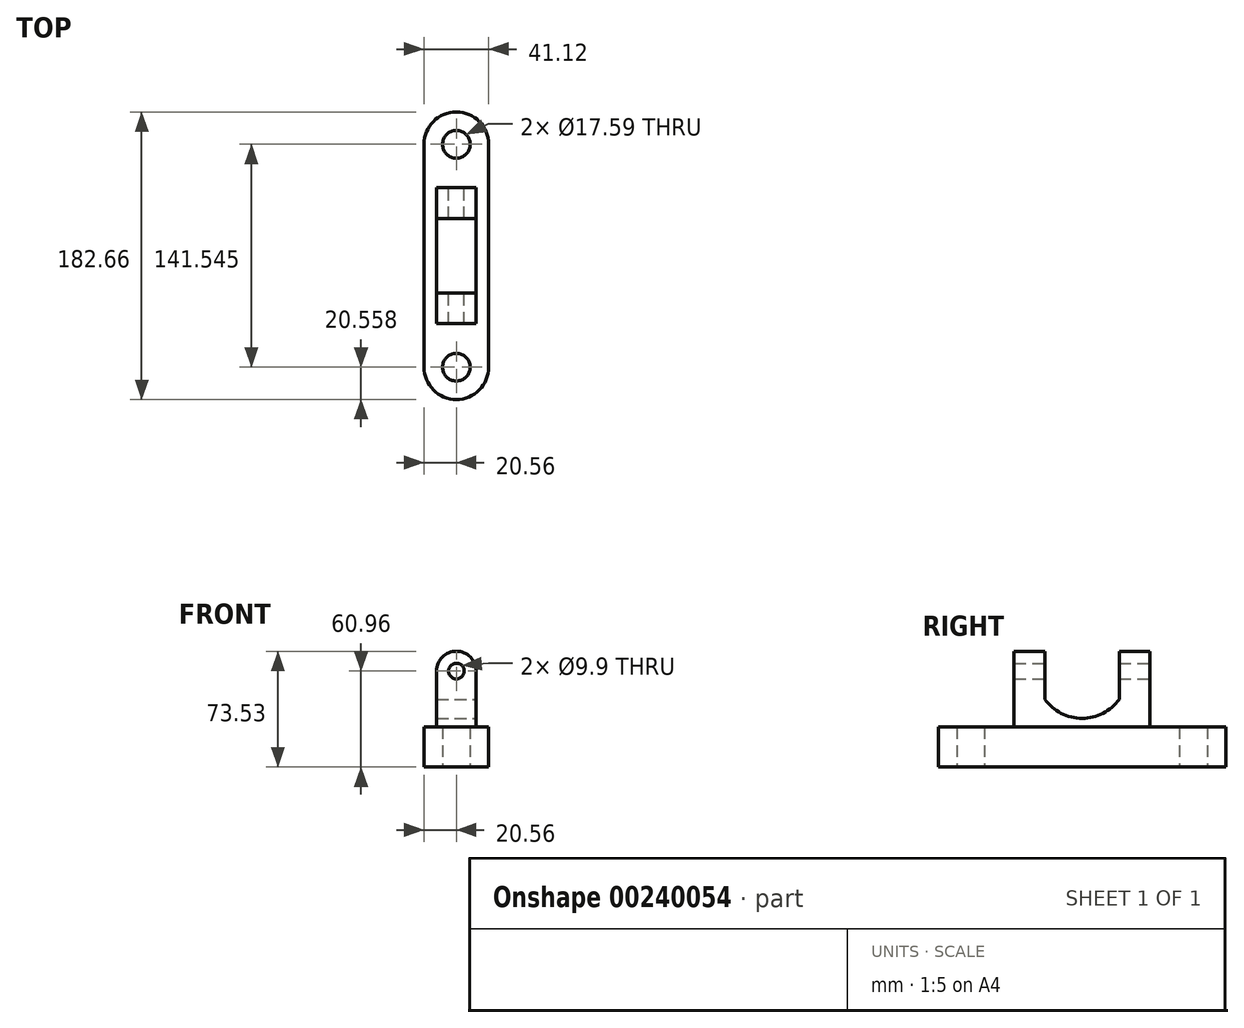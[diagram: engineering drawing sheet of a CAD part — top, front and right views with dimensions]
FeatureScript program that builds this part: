
annotation { "Feature Type Name" : "Feature", "Feature Type Description" : "" }
export const myFeature = defineFeature(function(context is Context, id is Id, definition is map)
    precondition{}
    {
        {
            var Q0;
            Q0=qCreatedBy(makeId("Top.planeOp"),FACE);
            var sketch = newSketch(context, id + "F0", { "sketchPlane" : qUnion([Q0])});
            skLineSegment(sketch, "E0.left", {"start": v(20.56, -70.77) * mm, "end": v(20.56, 70.77) * mm});
            skLineSegment(sketch, "E0.right", {"start": v(-20.56, -70.77) * mm, "end": v(-20.56, 70.77) * mm});
            skPoint(sketch, "E0.middle", {"position": v(0, 0) * mm});
            skArc(sketch, "E1", {"start": v(20.56, 70.77) * mm, "mid": v(0, 91.33) * mm, "end": v(-20.56, 70.77) * mm});
            skArc(sketch, "E2", {"start": v(-20.56, -70.77) * mm, "mid": v(0, -91.33) * mm, "end": v(20.56, -70.77) * mm});
            skCircle(sketch, "E3", {"center": v(0, 70.77) * mm, "radius": 8.8 * mm});
            skCircle(sketch, "E4.MirrorC", {"center": v(0, -70.77) * mm, "radius": 8.8 * mm});
            skSolve(sketch);
        }
        {
            var Q0;
            Q0=makeQuery(id+"F0.imprint","IMPRINT",FACE,{"disambiguationData":[TD([[makeQuery(id+"F0.imprint","IMPRINT",EDGE,{"derivedFrom":sQuery(id+"F0.wireOp",EDGE,"E0.left")}),1.0]])]});
            extrude(context, id + "F1", {"entities" : qUnion([Q0]), "depth" : 25.4 * mm});
        }
        {
            var Q0;
            Q0=qCreatedBy(makeId("Front.planeOp"),FACE);
            var sketch = newSketch(context, id + "F2", { "sketchPlane" : qUnion([Q0])});
            skLineSegment(sketch, "E5", {"start": v(0, 0) * mm, "end": v(0, 25.4) * mm, "construction": true});
            skLineSegment(sketch, "E6", {"start": v(0, 25.4) * mm, "end": v(-12.57, 25.4) * mm});
            skLineSegment(sketch, "E7.MirrorCS", {"start": v(0, 25.4) * mm, "end": v(12.57, 25.4) * mm});
            skLineSegment(sketch, "E8", {"start": v(12.57, 25.4) * mm, "end": v(12.57, 60.96) * mm});
            skLineSegment(sketch, "E9", {"start": v(-12.57, 60.96) * mm, "end": v(-12.57, 25.4) * mm});
            skArc(sketch, "E10", {"start": v(12.57, 60.96) * mm, "mid": v(0, 73.53) * mm, "end": v(-12.57, 60.96) * mm});
            skCircle(sketch, "E11", {"center": v(0, 60.96) * mm, "radius": 4.95 * mm});
            skSolve(sketch);
        }
        {
            var Q0;
            Q0=makeQuery(id+"F2.imprint","IMPRINT",FACE,{"disambiguationData":[TD([[makeQuery(id+"F2.imprint","IMPRINT",EDGE,{"derivedFrom":sQuery(id+"F2.wireOp",EDGE,"E6")}),-1.0]])]});
            extrude(context, id + "F3", {"entities" : qUnion([Q0]), "operationType" : NewBodyOperationType.ADD, "depth" : 43.18 * mm, "hasSecondDirection" : true, "secondDirectionOppositeDirection" : true, "secondDirectionDepth" : 43.18 * mm});
        }
        {
            var Q0;
            Q0=qCreatedBy(makeId("Right.planeOp"),FACE);
            var sketch = newSketch(context, id + "F4", { "sketchPlane" : qUnion([Q0])});
            skLineSegment(sketch, "E12", {"start": v(0, 0) * mm, "end": v(0, 73.3) * mm, "construction": true});
            skLineSegment(sketch, "E13", {"start": v(-23.65, 93.86) * mm, "end": v(-23.65, 43.06) * mm});
            skLineSegment(sketch, "E14", {"start": v(23.65, 43.06) * mm, "end": v(23.65, 93.86) * mm});
            skArc(sketch, "E15", {"start": v(-23.65, 43.06) * mm, "mid": v(0, 30.99) * mm, "end": v(23.65, 43.06) * mm});
            skLineSegment(sketch, "E16", {"start": v(-23.65, 93.86) * mm, "end": v(23.65, 93.86) * mm});
            skSolve(sketch);
        }
        {
            var Q0;
            Q0 = qSketchRegion(id + "F4", true);
            extrude(context, id + "F5", {"entities" : qUnion([Q0]), "operationType" : NewBodyOperationType.REMOVE, "oppositeDirection" : true, "depth" : 25.4 * mm, "hasSecondDirection" : true, "secondDirectionOppositeDirection" : false, "secondDirectionDepth" : 25.4 * mm});
        }
    });
